# Revit family: ITK Ролик с тормозом
name_source: partatom
category: Обобщенные модели
revit_build: Autodesk Revit 2016 (Build: 20160314_0715(x64)
units: mm (PartAtom-declared; Revit-internal decimal feet)

## family parameters
Всегда вертикально = Да
Может служить основой для арматурных стержней = Нет
На основе рабочей плоскости = Нет
Общий = Нет
При загрузке вырезать с полостями = Нет
Размер круглого соединителя = Использовать диаметр
Тип детали = Нормальный
Точка расчета площади = Нет

## types (1)
- ITK-HP-25
    ADSK_Единица измерения = шт
    ADSK_Завод-изготовитель = IEK
    ADSK_Марка = ITK-HP-25
    ADSK_Масса = 0
    ADSK_Наименование = ITK Ролики с тормозом (1 шт)
    ADSK_Наименование краткое = ITK-HP-25
    URL = http://www.itk-group.ru
    Изготовитель = ITK
    Материал = Окраска - RAL 9005
    Описание = Шкафы и стойки ITK могут быть установлены на ножки или ролики, или на ножки и ролики одновременно. Ролики значительно снижают максимально возможную статическую нагрузку шкафа или стойки, но позволяют легко перемещать конструктив по помещению. При необходимости, ролики могут быть заблокированы ножным тормозом.

Ножки имеют регулировку высоты, с помощью которой можно нивелировать шкаф на не ровном полу.

Ролики и ножки устанавливаются в нижнем основании. Ножка вкручивается в отверстие, рассчитанное на резьбу М12. Ролик крепится с помощью 4 винтов. Колесо ролика и основание ножки имеют резиновое диэлектрическое покрытие, предотвращающее проводимость тока с корпуса на пол.
Совместимы со всеми 19-дюймовыми шкафами и стойками ITK.
Обладают современным привлекательным дизайном и продуманной конструкцией.
Удобны в монтаже и эксплуатации.
Соответствие международным стандартам ISO9001, IEC 297, ISO/IEC 11801. 
Сертифицированы по ГОСТ Р.
Все аксессуары идут с крепежом.
Возможно исполнение в двух цветах: серый (RAL7035) и черный (RAL9005).
Всегда в наличии на складе.
Гарантия на все аксессуары до 2-х лет.
    Совместимость = серия Linea F
